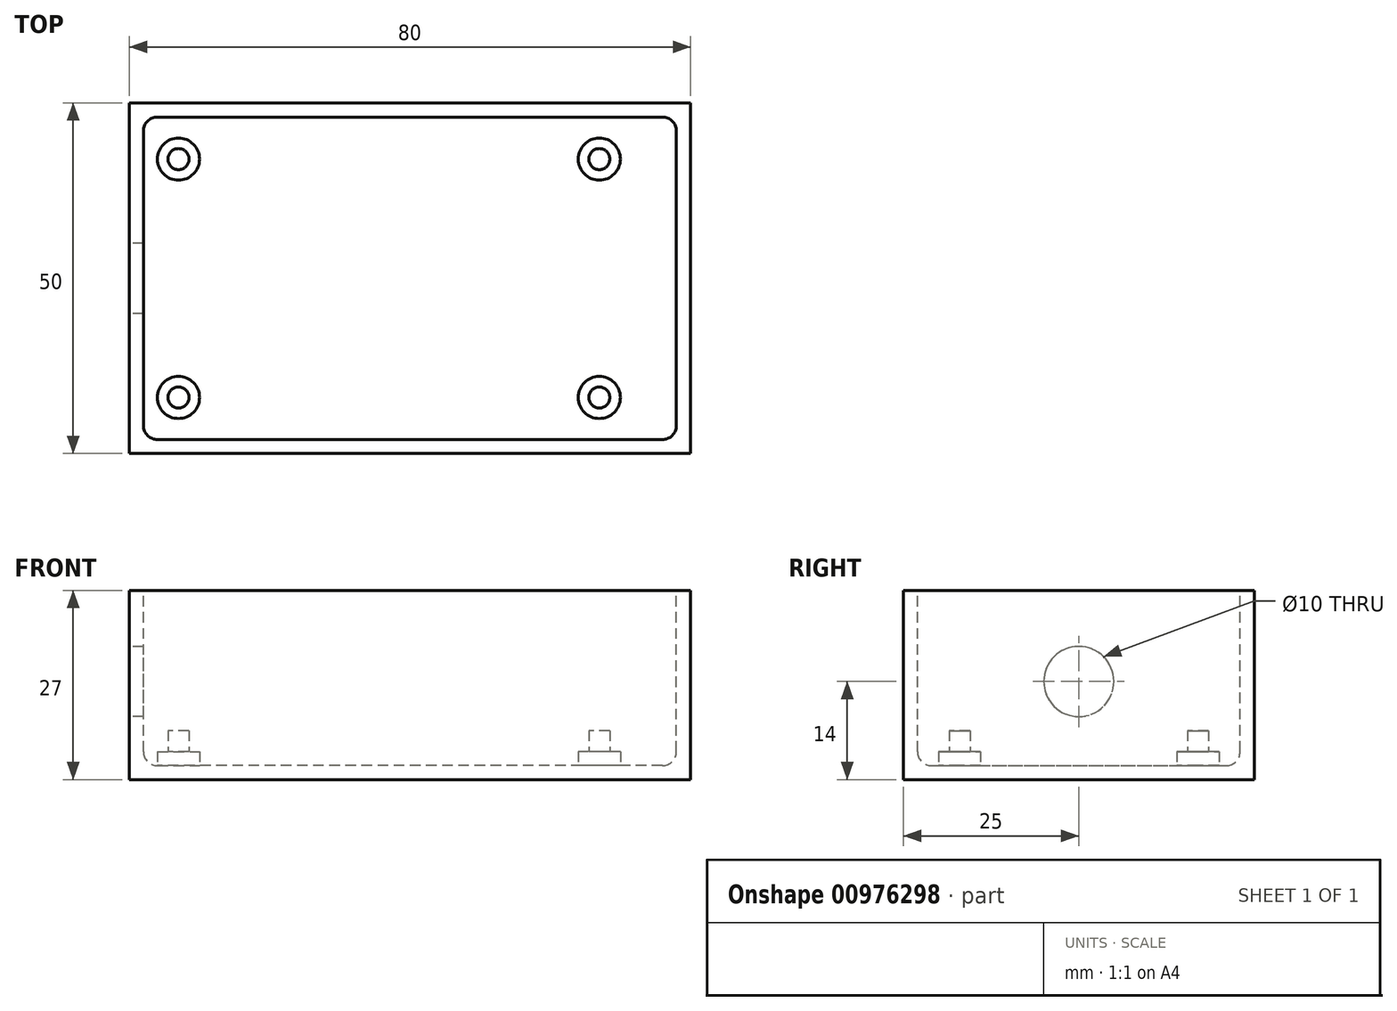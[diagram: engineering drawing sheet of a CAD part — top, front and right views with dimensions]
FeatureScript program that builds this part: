
annotation { "Feature Type Name" : "Feature", "Feature Type Description" : "" }
export const myFeature = defineFeature(function(context is Context, id is Id, definition is map)
    precondition{}
    {
        {
            var Q0;
            Q0=qCreatedBy(makeId("Top.planeOp"),FACE);
            var sketch = newSketch(context, id + "F0", { "sketchPlane" : qUnion([Q0])});
            skLineSegment(sketch, "E0.bottom", {"start": v(40, -25) * mm, "end": v(-40, -25) * mm});
            skLineSegment(sketch, "E0.top", {"start": v(40, 25) * mm, "end": v(-40, 25) * mm});
            skLineSegment(sketch, "E0.left", {"start": v(40, -25) * mm, "end": v(40, 25) * mm});
            skLineSegment(sketch, "E0.right", {"start": v(-40, -25) * mm, "end": v(-40, 25) * mm});
            skPoint(sketch, "E0.middle", {"position": v(0, 0) * mm});
            skSolve(sketch);
        }
        {
            var Q0;
            Q0 = qSketchRegion(id + "F0", true);
            extrude(context, id + "F1", {"entities" : qUnion([Q0]), "depth" : 27 * mm, "offsetDistance" : 25 * mm});
        }
        {
            var Q0;
            Q0=makeQuery(id+"F1.opExtrude","CAP_FACE",FACE,{"disambiguationData":[OSD([sQuery(id+"F0.wireOp",EDGE,"E0.bottom"),sQuery(id+"F0.wireOp",EDGE,"E0.top"),sQuery(id+"F0.wireOp",EDGE,"E0.left"),sQuery(id+"F0.wireOp",EDGE,"E0.right")])],"isStart":false});
            var sketch = newSketch(context, id + "F2", { "sketchPlane" : qUnion([Q0])});
            skLineSegment(sketch, "E1.bottom", {"start": v(38, -23) * mm, "end": v(-38, -23) * mm});
            skLineSegment(sketch, "E1.top", {"start": v(38, 23) * mm, "end": v(-38, 23) * mm});
            skLineSegment(sketch, "E1.left", {"start": v(38, -23) * mm, "end": v(38, 23) * mm});
            skLineSegment(sketch, "E1.right", {"start": v(-38, -23) * mm, "end": v(-38, 23) * mm});
            skPoint(sketch, "E1.middle", {"position": v(0, 0) * mm});
            skSolve(sketch);
        }
        {
            var Q0;
            Q0=makeQuery(id+"F2.imprint","IMPRINT",FACE,{"disambiguationData":[TD([[makeQuery(id+"F2.imprint","IMPRINT",EDGE,{"derivedFrom":sQuery(id+"F2.wireOp",EDGE,"E1.bottom")}),-1.0]])]});
            extrude(context, id + "F3", {"entities" : qUnion([Q0]), "operationType" : NewBodyOperationType.REMOVE, "oppositeDirection" : true, "depth" : 25 * mm, "offsetDistance" : 25 * mm});
        }
        {
            var Q0;
            Q0=makeQuery(id+"F3.boolean.opBoolean","COPY",FACE,{"derivedFrom":makeQuery(id+"F3.opExtrude","CAP_FACE",FACE,{"disambiguationData":[OSD([sQuery(id+"F2.wireOp",EDGE,"E1.bottom"),sQuery(id+"F2.wireOp",EDGE,"E1.top"),sQuery(id+"F2.wireOp",EDGE,"E1.left"),sQuery(id+"F2.wireOp",EDGE,"E1.right")])],"isStart":false})});
            var sketch = newSketch(context, id + "F4", { "sketchPlane" : qUnion([Q0])});
            skCircle(sketch, "E2", {"center": v(27, 17) * mm, "radius": 3 * mm});
            skCircle(sketch, "E3", {"center": v(27, -17) * mm, "radius": 3 * mm});
            skCircle(sketch, "E4", {"center": v(-33, 17) * mm, "radius": 3 * mm});
            skCircle(sketch, "E5", {"center": v(-33, -17) * mm, "radius": 3 * mm});
            skSolve(sketch);
        }
        {
            var Q0;
            Q0=makeQuery(id+"F4.imprint","IMPRINT",FACE,{"disambiguationData":[TD([[makeQuery(id+"F4.imprint","IMPRINT",EDGE,{"derivedFrom":sQuery(id+"F4.wireOp",EDGE,"E4")}),1.0]])]});
            var Q1;
            Q1=makeQuery(id+"F4.imprint","IMPRINT",FACE,{"disambiguationData":[TD([[makeQuery(id+"F4.imprint","IMPRINT",EDGE,{"derivedFrom":sQuery(id+"F4.wireOp",EDGE,"E2")}),1.0]])]});
            var Q2;
            Q2=makeQuery(id+"F4.imprint","IMPRINT",FACE,{"disambiguationData":[TD([[makeQuery(id+"F4.imprint","IMPRINT",EDGE,{"derivedFrom":sQuery(id+"F4.wireOp",EDGE,"E3")}),1.0]])]});
            var Q3;
            Q3=makeQuery(id+"F4.imprint","IMPRINT",FACE,{"disambiguationData":[TD([[makeQuery(id+"F4.imprint","IMPRINT",EDGE,{"derivedFrom":sQuery(id+"F4.wireOp",EDGE,"E5")}),1.0]])]});
            extrude(context, id + "F5", {"entities" : qUnion([Q0, Q1, Q2, Q3]), "operationType" : NewBodyOperationType.ADD, "depth" : 2 * mm, "offsetDistance" : 25 * mm});
        }
        {
            var Q0;
            Q0=makeQuery(id+"F5.opExtrude","CAP_FACE",FACE,{"disambiguationData":[OSD([sQuery(id+"F4.wireOp",EDGE,"E4")])],"isStart":false});
            var sketch = newSketch(context, id + "F6", { "sketchPlane" : qUnion([Q0])});
            skCircle(sketch, "E6", {"center": v(-33, 17) * mm, "radius": 1.5 * mm});
            skCircle(sketch, "E7", {"center": v(27, 17) * mm, "radius": 1.5 * mm});
            skCircle(sketch, "E8", {"center": v(27, -17) * mm, "radius": 1.5 * mm});
            skCircle(sketch, "E9", {"center": v(-33, -17) * mm, "radius": 1.5 * mm});
            skSolve(sketch);
        }
        {
            var Q0;
            Q0=makeQuery(id+"F6.imprint","IMPRINT",FACE,{"disambiguationData":[TD([[makeQuery(id+"F6.imprint","IMPRINT",EDGE,{"derivedFrom":sQuery(id+"F6.wireOp",EDGE,"E6")}),1.0]])]});
            var Q1;
            Q1=makeQuery(id+"F6.imprint","IMPRINT",FACE,{"disambiguationData":[TD([[makeQuery(id+"F6.imprint","IMPRINT",EDGE,{"derivedFrom":sQuery(id+"F6.wireOp",EDGE,"E7")}),1.0]])]});
            var Q2;
            Q2=makeQuery(id+"F6.imprint","IMPRINT",FACE,{"disambiguationData":[TD([[makeQuery(id+"F6.imprint","IMPRINT",EDGE,{"derivedFrom":sQuery(id+"F6.wireOp",EDGE,"E8")}),1.0]])]});
            var Q3;
            Q3=makeQuery(id+"F6.imprint","IMPRINT",FACE,{"disambiguationData":[TD([[makeQuery(id+"F6.imprint","IMPRINT",EDGE,{"derivedFrom":sQuery(id+"F6.wireOp",EDGE,"E9")}),1.0]])]});
            extrude(context, id + "F7", {"entities" : qUnion([Q0, Q1, Q2, Q3]), "depth" : 3 * mm, "offsetDistance" : 25 * mm});
        }
        {
            var Q0;
            Q0=makeQuery(id+"F1.opExtrude","SWEPT_FACE",FACE,{"disambiguationData":[OSD([sQuery(id+"F0.wireOp",EDGE,"E0.right")])]});
            var sketch = newSketch(context, id + "F8", { "sketchPlane" : qUnion([Q0])});
            skCircle(sketch, "E10", {"center": v(0, 14) * mm, "radius": 5 * mm});
            skSolve(sketch);
        }
        {
            var Q0;
            Q0=makeQuery(id+"F8.imprint","IMPRINT",FACE,{"disambiguationData":[TD([[makeQuery(id+"F8.imprint","IMPRINT",EDGE,{"derivedFrom":sQuery(id+"F8.wireOp",EDGE,"E10")}),1.0]])]});
            extrude(context, id + "F9", {"entities" : qUnion([Q0]), "operationType" : NewBodyOperationType.REMOVE, "oppositeDirection" : true, "depth" : 25 * mm, "offsetDistance" : 25 * mm});
        }
        {
            var Q0;
            Q0=makeQuery(id+"F3.boolean.opBoolean","COPY",EDGE,{"derivedFrom":makeQuery(id+"F3.opExtrude","SWEPT_EDGE",EDGE,{"disambiguationData":[OSD([sQuery(id+"F2.wireOp",EDGE,"E1.top"),sQuery(id+"F2.wireOp",EDGE,"E1.right")])]})});
            var Q1;
            Q1=makeQuery(id+"F3.boolean.opBoolean","COPY",EDGE,{"derivedFrom":makeQuery(id+"F3.opExtrude","SWEPT_EDGE",EDGE,{"disambiguationData":[OSD([sQuery(id+"F2.wireOp",EDGE,"E1.top"),sQuery(id+"F2.wireOp",EDGE,"E1.left")])]})});
            var Q2;
            Q2=makeQuery(id+"F3.boolean.opBoolean","COPY",EDGE,{"derivedFrom":makeQuery(id+"F3.opExtrude","SWEPT_EDGE",EDGE,{"disambiguationData":[OSD([sQuery(id+"F2.wireOp",EDGE,"E1.bottom"),sQuery(id+"F2.wireOp",EDGE,"E1.left")])]})});
            var Q3;
            Q3=makeQuery(id+"F3.boolean.opBoolean","COPY",EDGE,{"derivedFrom":makeQuery(id+"F3.opExtrude","SWEPT_EDGE",EDGE,{"disambiguationData":[OSD([sQuery(id+"F2.wireOp",EDGE,"E1.bottom"),sQuery(id+"F2.wireOp",EDGE,"E1.right")])]})});
            var Q4;
            Q4=makeQuery(id+"F3.boolean.opBoolean","COPY",EDGE,{"derivedFrom":makeQuery(id+"F3.opExtrude","CAP_EDGE",EDGE,{"disambiguationData":[OSD([sQuery(id+"F2.wireOp",EDGE,"E1.top")])],"isStart":false})});
            var Q5;
            Q5=makeQuery(id+"F3.boolean.opBoolean","COPY",EDGE,{"derivedFrom":makeQuery(id+"F3.opExtrude","CAP_EDGE",EDGE,{"disambiguationData":[OSD([sQuery(id+"F2.wireOp",EDGE,"E1.left")])],"isStart":false})});
            var Q6;
            Q6=makeQuery(id+"F3.boolean.opBoolean","COPY",EDGE,{"derivedFrom":makeQuery(id+"F3.opExtrude","CAP_EDGE",EDGE,{"disambiguationData":[OSD([sQuery(id+"F2.wireOp",EDGE,"E1.bottom")])],"isStart":false})});
            var Q7;
            Q7=makeQuery(id+"F3.boolean.opBoolean","COPY",EDGE,{"derivedFrom":makeQuery(id+"F3.opExtrude","CAP_EDGE",EDGE,{"disambiguationData":[OSD([sQuery(id+"F2.wireOp",EDGE,"E1.right")])],"isStart":false})});
            fillet(context, id + "F10", {"entities" : qUnion([Q0, Q1, Q2, Q3, Q4, Q5, Q6, Q7]), "radius" : 2 * mm, "tangentPropagation" : true, "allowEdgeOverflow" : false});
        }
    });
